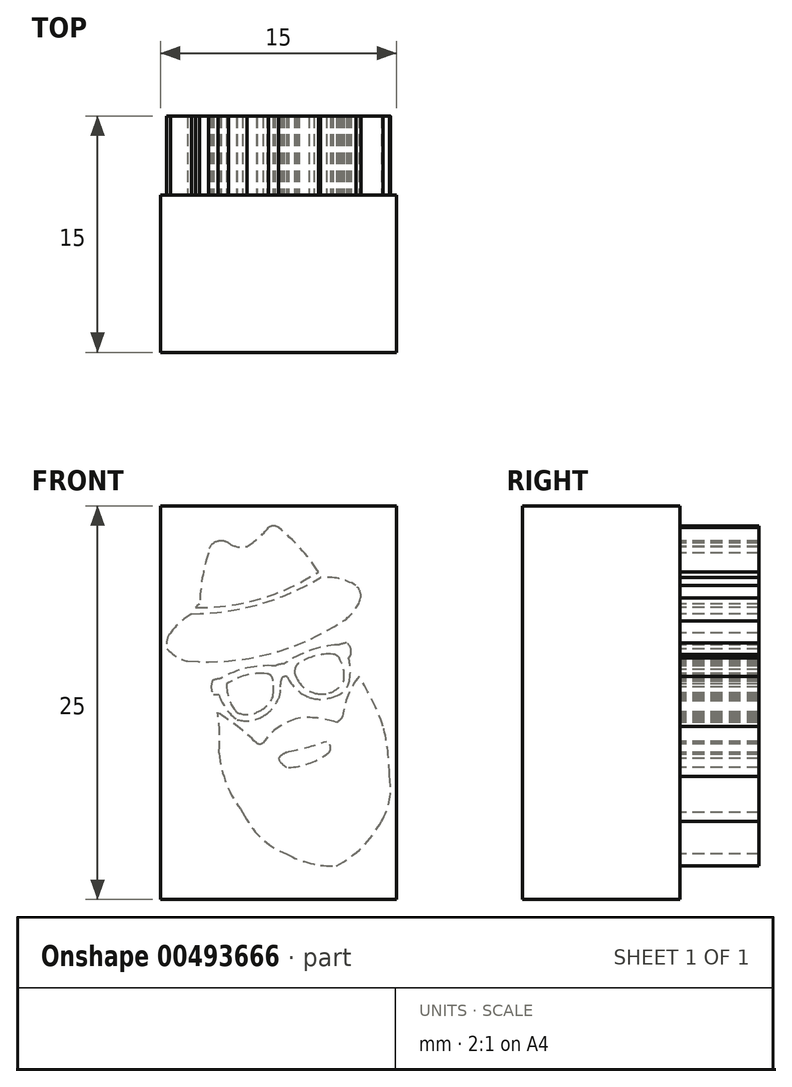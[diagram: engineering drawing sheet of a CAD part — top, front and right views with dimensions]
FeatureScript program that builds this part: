
annotation { "Feature Type Name" : "Feature", "Feature Type Description" : "" }
export const myFeature = defineFeature(function(context is Context, id is Id, definition is map)
    precondition{}
    {
        {
            var Q0;
            Q0=qCreatedBy(makeId("Front.planeOp"),FACE);
            var sketch = newSketch(context, id + "F0", { "sketchPlane" : qUnion([Q0])});
            skLineSegment(sketch, "E0.bottom", {"start": v(7.5, 12.5) * mm, "end": v(-7.5, 12.5) * mm});
            skLineSegment(sketch, "E0.top", {"start": v(7.5, -12.5) * mm, "end": v(-7.5, -12.5) * mm});
            skLineSegment(sketch, "E0.left", {"start": v(7.5, 12.5) * mm, "end": v(7.5, -12.5) * mm});
            skLineSegment(sketch, "E0.right", {"start": v(-7.5, 12.5) * mm, "end": v(-7.5, -12.5) * mm});
            skPoint(sketch, "E0.middle", {"position": v(0, 0) * mm});
            skArc(sketch, "E1", {"start": v(-5.25, 6.04) * mm, "mid": v(-1.2, 6.58) * mm, "end": v(2.53, 8.31) * mm});
            skArc(sketch, "E2", {"start": v(2.53, 8.31) * mm, "mid": v(1.37, 9.81) * mm, "end": v(0, 11.11) * mm});
            skArc(sketch, "E3", {"start": v(0, 11.11) * mm, "mid": v(-0.32, 11.22) * mm, "end": v(-0.63, 11.11) * mm});
            skArc(sketch, "E4", {"start": v(-2, 9.93) * mm, "mid": v(-1.26, 10.46) * mm, "end": v(-0.63, 11.11) * mm});
            skArc(sketch, "E5", {"start": v(-3.18, 10.14) * mm, "mid": v(-2.61, 9.9) * mm, "end": v(-2, 9.93) * mm});
            skArc(sketch, "E6", {"start": v(-3.18, 10.14) * mm, "mid": v(-3.5, 10.26) * mm, "end": v(-3.84, 10.25) * mm});
            skArc(sketch, "E7", {"start": v(-3.84, 10.25) * mm, "mid": v(-4.28, 9.99) * mm, "end": v(-4.45, 9.5) * mm});
            skArc(sketch, "E8", {"start": v(-5, 6.26) * mm, "mid": v(-5.15, 6.17) * mm, "end": v(-5.25, 6.04) * mm});
            skArc(sketch, "E9", {"start": v(-4.45, 9.5) * mm, "mid": v(-4.84, 7.9) * mm, "end": v(-5, 6.26) * mm});
            skArc(sketch, "E10", {"start": v(-5.5, 5.63) * mm, "mid": v(-1.26, 6.24) * mm, "end": v(2.67, 7.95) * mm});
            skArc(sketch, "E11", {"start": v(4.91, 7.44) * mm, "mid": v(3.83, 7.87) * mm, "end": v(2.67, 7.95) * mm});
            skArc(sketch, "E12", {"start": v(5.22, 6.64) * mm, "mid": v(5.17, 7.08) * mm, "end": v(4.91, 7.44) * mm});
            skArc(sketch, "E13", {"start": v(4.1, 5.2) * mm, "mid": v(4.8, 5.81) * mm, "end": v(5.22, 6.64) * mm});
            skArc(sketch, "E14", {"start": v(-5.77, 2.64) * mm, "mid": v(-0.61, 3.09) * mm, "end": v(4.1, 5.2) * mm});
            skArc(sketch, "E15", {"start": v(-7.07, 3.42) * mm, "mid": v(-6.49, 2.9) * mm, "end": v(-5.77, 2.64) * mm});
            skArc(sketch, "E16", {"start": v(-6.86, 4.42) * mm, "mid": v(-7.09, 3.95) * mm, "end": v(-7.07, 3.42) * mm});
            skArc(sketch, "E17", {"start": v(-5.5, 5.63) * mm, "mid": v(-6.25, 5.1) * mm, "end": v(-6.86, 4.42) * mm});
            skArc(sketch, "E18", {"start": v(3.8, 3.66) * mm, "mid": v(1.99, 3.3) * mm, "end": v(0.34, 2.46) * mm});
            skArc(sketch, "E19", {"start": v(0.34, 2.46) * mm, "mid": v(0.05, 2.42) * mm, "end": v(-0.23, 2.32) * mm});
            skArc(sketch, "E20", {"start": v(-0.23, 2.32) * mm, "mid": v(-2, 2.2) * mm, "end": v(-3.67, 1.52) * mm});
            skArc(sketch, "E21", {"start": v(-3.67, 1.52) * mm, "mid": v(-3.93, 1.48) * mm, "end": v(-4.2, 1.4) * mm});
            skArc(sketch, "E22", {"start": v(4.33, 3.79) * mm, "mid": v(4.06, 3.74) * mm, "end": v(3.8, 3.66) * mm});
            skArc(sketch, "E23", {"start": v(4.6, 3.05) * mm, "mid": v(4.58, 3.46) * mm, "end": v(4.33, 3.79) * mm});
            skArc(sketch, "E24", {"start": v(4.45, 2.84) * mm, "mid": v(4.53, 2.94) * mm, "end": v(4.6, 3.05) * mm});
            skArc(sketch, "E25", {"start": v(4.45, 1.17) * mm, "mid": v(4.56, 2) * mm, "end": v(4.45, 2.84) * mm});
            skArc(sketch, "E26", {"start": v(3.4, 0.34) * mm, "mid": v(4.03, 0.62) * mm, "end": v(4.45, 1.17) * mm});
            skArc(sketch, "E27", {"start": v(1.93, 0.34) * mm, "mid": v(2.67, 0.21) * mm, "end": v(3.4, 0.34) * mm});
            skArc(sketch, "E28", {"start": v(0.57, 1.63) * mm, "mid": v(1.12, 0.85) * mm, "end": v(1.93, 0.34) * mm});
            skArc(sketch, "E29", {"start": v(0.57, 1.63) * mm, "mid": v(0.38, 1.64) * mm, "end": v(0.21, 1.57) * mm});
            skArc(sketch, "E30", {"start": v(0.21, 1.57) * mm, "mid": v(0.14, 1.3) * mm, "end": v(0.1, 1) * mm});
            skArc(sketch, "E31", {"start": v(-0.08, 0.09) * mm, "mid": v(0.1, 0.53) * mm, "end": v(0.1, 1) * mm});
            skArc(sketch, "E32", {"start": v(-0.98, -0.87) * mm, "mid": v(-0.46, -0.46) * mm, "end": v(-0.08, 0.09) * mm});
            skArc(sketch, "E33", {"start": v(-2.63, -1.09) * mm, "mid": v(-1.78, -1.14) * mm, "end": v(-0.98, -0.87) * mm});
            skArc(sketch, "E34", {"start": v(-3.79, 0.47) * mm, "mid": v(-3.33, -0.4) * mm, "end": v(-2.63, -1.09) * mm});
            skArc(sketch, "E35", {"start": v(-3.79, 0.47) * mm, "mid": v(-3.96, 0.49) * mm, "end": v(-4.14, 0.47) * mm});
            skArc(sketch, "E36", {"start": v(-4.2, 1.4) * mm, "mid": v(-4.27, 0.93) * mm, "end": v(-4.14, 0.47) * mm});
            skArc(sketch, "E37", {"start": v(6.65, -1.5) * mm, "mid": v(5.97, 0.12) * mm, "end": v(5.11, 1.66) * mm});
            skArc(sketch, "E38", {"start": v(5.11, 1.66) * mm, "mid": v(4.41, 0.47) * mm, "end": v(4.08, -0.87) * mm});
            skArc(sketch, "E39", {"start": v(3.67, -1.25) * mm, "mid": v(3.9, -1.1) * mm, "end": v(4.08, -0.87) * mm});
            skArc(sketch, "E40", {"start": v(3.67, -1.25) * mm, "mid": v(2.48, -0.99) * mm, "end": v(1.25, -1) * mm});
            skArc(sketch, "E41", {"start": v(1.25, -1) * mm, "mid": v(-0.01, -1.57) * mm, "end": v(-0.98, -2.57) * mm});
            skArc(sketch, "E42", {"start": v(-1.4, -2.57) * mm, "mid": v(-1.2, -2.62) * mm, "end": v(-0.98, -2.57) * mm});
            skArc(sketch, "E43", {"start": v(-1.4, -2.57) * mm, "mid": v(-2.59, -1.52) * mm, "end": v(-3.88, -0.63) * mm});
            skArc(sketch, "E44", {"start": v(-3.79, -3.2) * mm, "mid": v(-3.73, -1.9) * mm, "end": v(-3.88, -0.63) * mm});
            skArc(sketch, "E45", {"start": v(-3.79, -3.2) * mm, "mid": v(-3.3, -5.19) * mm, "end": v(-2.27, -6.97) * mm});
            skArc(sketch, "E46", {"start": v(-2.27, -6.97) * mm, "mid": v(-1.14, -8.57) * mm, "end": v(0.5, -9.61) * mm});
            skArc(sketch, "E47", {"start": v(0.5, -9.61) * mm, "mid": v(2.04, -10.21) * mm, "end": v(3.67, -10.38) * mm});
            skArc(sketch, "E48", {"start": v(3.67, -10.38) * mm, "mid": v(5.32, -9.18) * mm, "end": v(6.53, -7.55) * mm});
            skArc(sketch, "E49", {"start": v(6.53, -7.55) * mm, "mid": v(7.05, -6.16) * mm, "end": v(7.05, -4.68) * mm});
            skArc(sketch, "E50", {"start": v(7.05, -4.68) * mm, "mid": v(6.94, -3.08) * mm, "end": v(6.65, -1.5) * mm});
            skArc(sketch, "E51", {"start": v(0.52, -3.15) * mm, "mid": v(1.8, -2.85) * mm, "end": v(3.03, -2.46) * mm});
            skArc(sketch, "E52", {"start": v(0.52, -3.15) * mm, "mid": v(0.23, -3.32) * mm, "end": v(0, -3.55) * mm});
            skArc(sketch, "E53", {"start": v(0, -3.55) * mm, "mid": v(0.25, -3.92) * mm, "end": v(0.63, -4.13) * mm});
            skArc(sketch, "E54", {"start": v(3.03, -3.3) * mm, "mid": v(3.3, -2.88) * mm, "end": v(3.03, -2.46) * mm});
            skArc(sketch, "E55", {"start": v(0.63, -4.13) * mm, "mid": v(1.9, -3.88) * mm, "end": v(3.03, -3.3) * mm});
            skArc(sketch, "E56", {"start": v(-0.74, 1.82) * mm, "mid": v(-2.08, 1.73) * mm, "end": v(-3.3, 1.17) * mm});
            skArc(sketch, "E57", {"start": v(-3.3, 1.17) * mm, "mid": v(-3.15, 0.22) * mm, "end": v(-2.66, -0.6) * mm});
            skArc(sketch, "E58", {"start": v(-2.66, -0.6) * mm, "mid": v(-2, -0.76) * mm, "end": v(-1.36, -0.6) * mm});
            skArc(sketch, "E59", {"start": v(-1.36, -0.6) * mm, "mid": v(-0.76, -0.23) * mm, "end": v(-0.36, 0.35) * mm});
            skArc(sketch, "E60", {"start": v(-0.36, 0.35) * mm, "mid": v(-0.32, 0.87) * mm, "end": v(-0.36, 1.38) * mm});
            skArc(sketch, "E61", {"start": v(-0.36, 1.38) * mm, "mid": v(-0.46, 1.69) * mm, "end": v(-0.74, 1.82) * mm});
            skArc(sketch, "E62", {"start": v(3.45, 3.07) * mm, "mid": v(2.32, 2.96) * mm, "end": v(1.3, 2.5) * mm});
            skArc(sketch, "E63", {"start": v(1.3, 2.5) * mm, "mid": v(1.11, 2.33) * mm, "end": v(1.03, 2.1) * mm});
            skArc(sketch, "E64", {"start": v(1.03, 2.1) * mm, "mid": v(1.05, 1.8) * mm, "end": v(1.18, 1.52) * mm});
            skArc(sketch, "E65", {"start": v(1.18, 1.52) * mm, "mid": v(1.62, 0.94) * mm, "end": v(2.27, 0.6) * mm});
            skArc(sketch, "E66", {"start": v(2.27, 0.6) * mm, "mid": v(2.74, 0.54) * mm, "end": v(3.22, 0.6) * mm});
            skArc(sketch, "E67", {"start": v(3.22, 0.6) * mm, "mid": v(3.75, 0.89) * mm, "end": v(4.13, 1.35) * mm});
            skArc(sketch, "E68", {"start": v(4.13, 1.35) * mm, "mid": v(4.15, 2.02) * mm, "end": v(3.93, 2.66) * mm});
            skArc(sketch, "E69", {"start": v(3.93, 2.66) * mm, "mid": v(3.76, 2.95) * mm, "end": v(3.45, 3.07) * mm});
            skSolve(sketch);
        }
        {
            var Q0;
            Q0=makeQuery(id+"F0.imprint","IMPRINT",FACE,{"disambiguationData":[TD([[makeQuery(id+"F0.imprint","IMPRINT",EDGE,{"derivedFrom":sQuery(id+"F0.wireOp",EDGE,"E1")}),1.0]])]});
            var Q1;
            Q1=makeQuery(id+"F0.imprint","IMPRINT",FACE,{"disambiguationData":[TD([[makeQuery(id+"F0.imprint","IMPRINT",EDGE,{"derivedFrom":sQuery(id+"F0.wireOp",EDGE,"E10")}),-1.0]])]});
            var Q2;
            Q2=makeQuery(id+"F0.imprint","IMPRINT",FACE,{"disambiguationData":[TD([[makeQuery(id+"F0.imprint","IMPRINT",EDGE,{"derivedFrom":sQuery(id+"F0.wireOp",EDGE,"E18")}),1.0]])]});
            var Q3;
            Q3=makeQuery(id+"F0.imprint","IMPRINT",FACE,{"disambiguationData":[TD([[makeQuery(id+"F0.imprint","IMPRINT",EDGE,{"derivedFrom":sQuery(id+"F0.wireOp",EDGE,"E37")}),1.0]])]});
            extrude(context, id + "F1", {"entities" : qUnion([Q0, Q1, Q2, Q3]), "oppositeDirection" : true, "depth" : 5 * mm});
        }
        {
            var Q0;
            Q0=makeQuery(id+"F0.imprint","IMPRINT",FACE,{"disambiguationData":[TD([[makeQuery(id+"F0.imprint","IMPRINT",EDGE,{"derivedFrom":sQuery(id+"F0.wireOp",EDGE,"E0.bottom")}),1.0]])]});
            var Q1;
            Q1=makeQuery(id+"F0.imprint","IMPRINT",FACE,{"disambiguationData":[TD([[makeQuery(id+"F0.imprint","IMPRINT",EDGE,{"derivedFrom":sQuery(id+"F0.wireOp",EDGE,"E1")}),1.0]])]});
            var Q2;
            Q2=makeQuery(id+"F0.imprint","IMPRINT",FACE,{"disambiguationData":[TD([[makeQuery(id+"F0.imprint","IMPRINT",EDGE,{"derivedFrom":sQuery(id+"F0.wireOp",EDGE,"E10")}),-1.0]])]});
            var Q3;
            Q3=makeQuery(id+"F0.imprint","IMPRINT",FACE,{"disambiguationData":[TD([[makeQuery(id+"F0.imprint","IMPRINT",EDGE,{"derivedFrom":sQuery(id+"F0.wireOp",EDGE,"E18")}),1.0]])]});
            var Q4;
            Q4=makeQuery(id+"F0.imprint","IMPRINT",FACE,{"disambiguationData":[TD([[makeQuery(id+"F0.imprint","IMPRINT",EDGE,{"derivedFrom":sQuery(id+"F0.wireOp",EDGE,"E37")}),1.0]])]});
            var Q5;
            Q5=makeQuery(id+"F0.imprint","IMPRINT",FACE,{"disambiguationData":[TD([[makeQuery(id+"F0.imprint","IMPRINT",EDGE,{"derivedFrom":sQuery(id+"F0.wireOp",EDGE,"E51")}),-1.0]])]});
            var Q6;
            Q6=makeQuery(id+"F0.imprint","IMPRINT",FACE,{"disambiguationData":[TD([[makeQuery(id+"F0.imprint","IMPRINT",EDGE,{"derivedFrom":sQuery(id+"F0.wireOp",EDGE,"E56")}),1.0]])]});
            var Q7;
            Q7=makeQuery(id+"F0.imprint","IMPRINT",FACE,{"disambiguationData":[TD([[makeQuery(id+"F0.imprint","IMPRINT",EDGE,{"derivedFrom":sQuery(id+"F0.wireOp",EDGE,"E62")}),1.0]])]});
            extrude(context, id + "F2", {"entities" : qUnion([Q0, Q1, Q2, Q3, Q4, Q5, Q6, Q7]), "operationType" : NewBodyOperationType.ADD, "depth" : 10 * mm});
        }
    });
